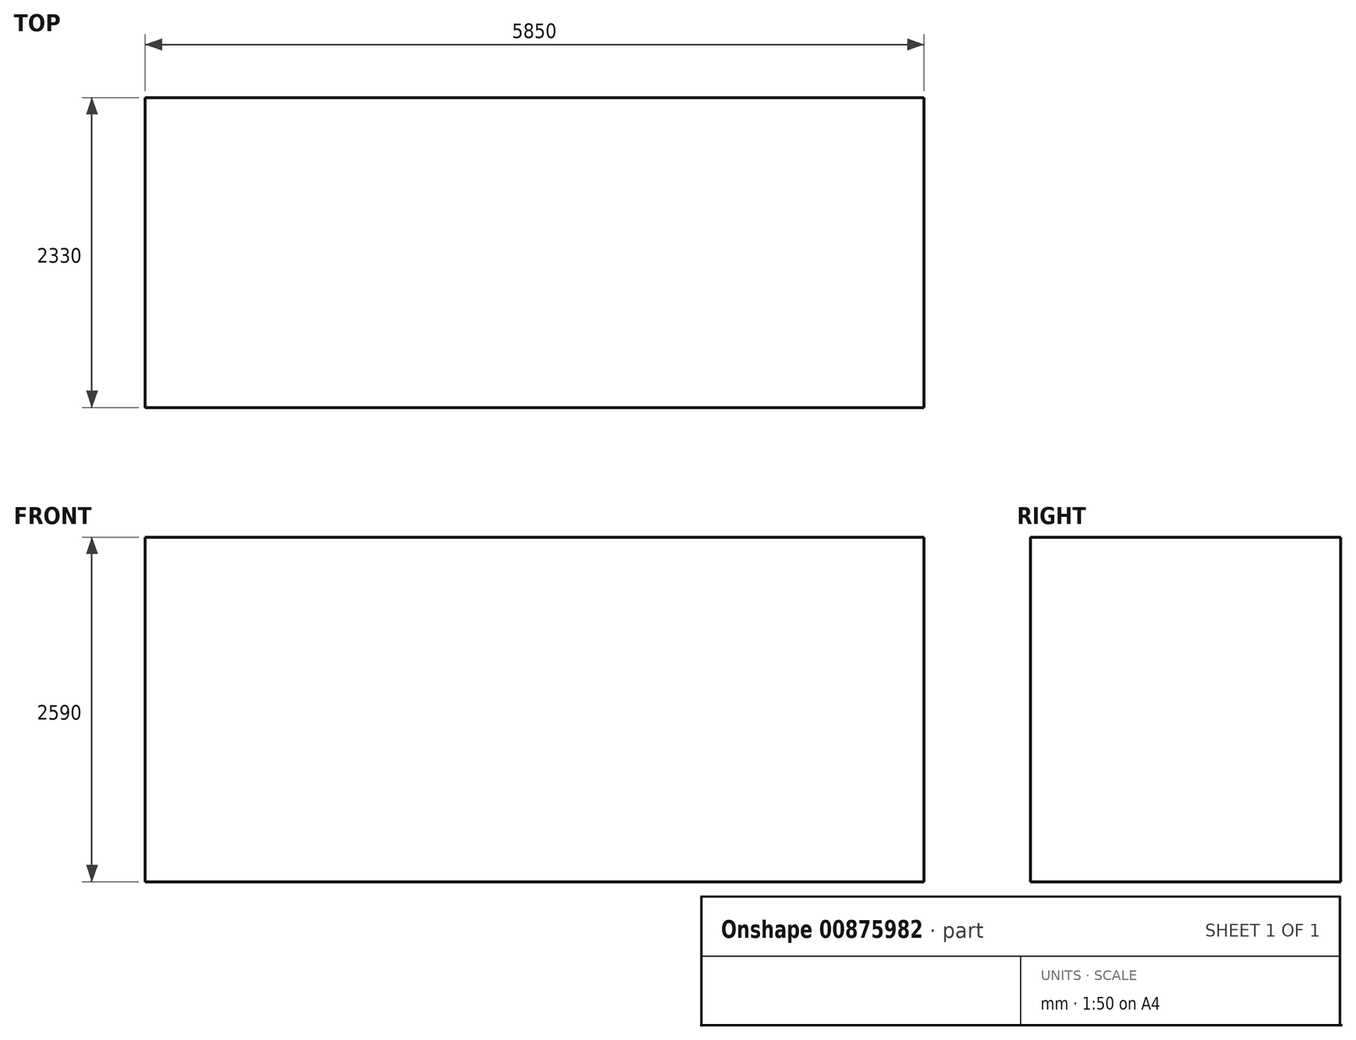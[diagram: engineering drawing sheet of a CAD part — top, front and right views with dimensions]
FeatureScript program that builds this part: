
annotation { "Feature Type Name" : "Feature", "Feature Type Description" : "" }
export const myFeature = defineFeature(function(context is Context, id is Id, definition is map)
    precondition{}
    {
        {
            var Q0;
            Q0=qCreatedBy(makeId("Top.planeOp"),FACE);
            var sketch = newSketch(context, id + "F0", { "sketchPlane" : qUnion([Q0])});
            skLineSegment(sketch, "E0.bottom", {"start": v(-2802.17, 1338.04) * mm, "end": v(3047.83, 1338.04) * mm});
            skLineSegment(sketch, "E0.top", {"start": v(-2802.17, -991.96) * mm, "end": v(3047.83, -991.96) * mm});
            skLineSegment(sketch, "E0.left", {"start": v(-2802.17, 1338.04) * mm, "end": v(-2802.17, -991.96) * mm});
            skLineSegment(sketch, "E0.right", {"start": v(3047.83, 1338.04) * mm, "end": v(3047.83, -991.96) * mm});
            skSolve(sketch);
        }
        {
            var Q0;
            Q0=makeQuery(id+"F0.imprint","IMPRINT",FACE,{"disambiguationData":[TD([[makeQuery(id+"F0.imprint","IMPRINT",EDGE,{"derivedFrom":sQuery(id+"F0.wireOp",EDGE,"E0.bottom")}),-1.0]])]});
            extrude(context, id + "F1", {"entities" : qUnion([Q0]), "depth" : 2590 * mm, "offsetDistance" : 25 * mm});
        }
    });
